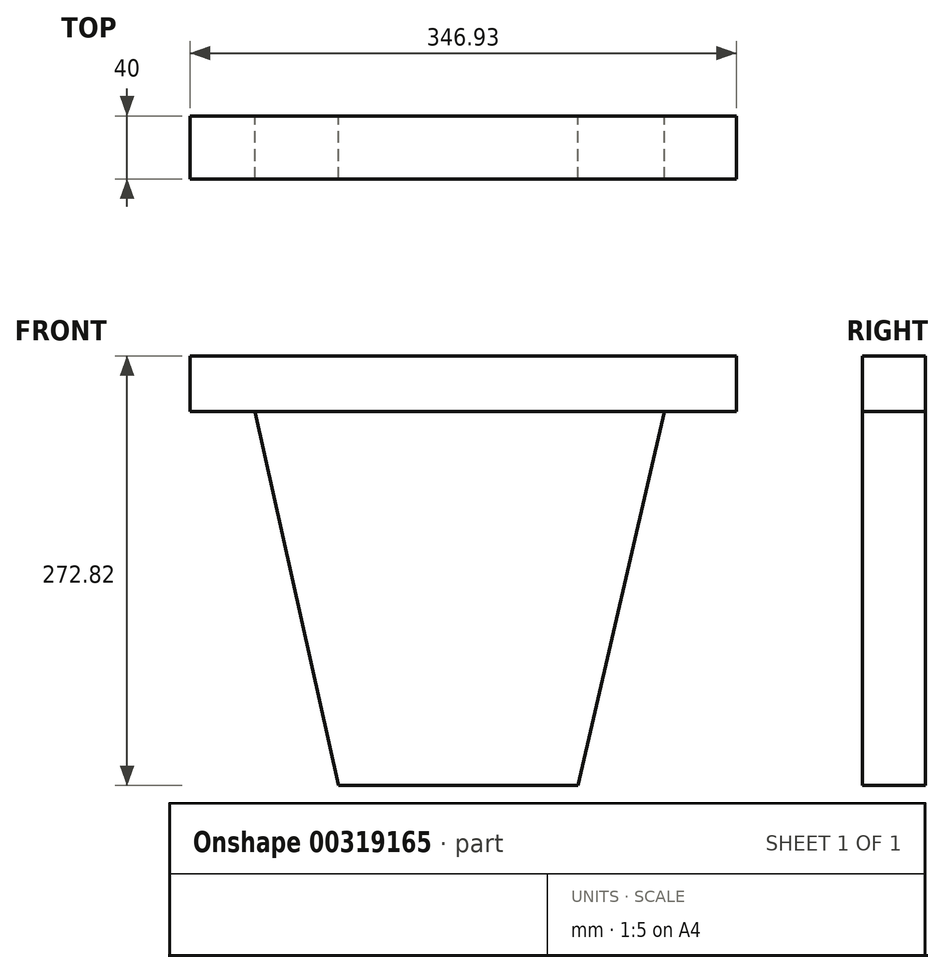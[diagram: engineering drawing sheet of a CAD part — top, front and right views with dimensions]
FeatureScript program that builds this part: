
annotation { "Feature Type Name" : "Feature", "Feature Type Description" : "" }
export const myFeature = defineFeature(function(context is Context, id is Id, definition is map)
    precondition{}
    {
        {
            var Q0;
            Q0=qCreatedBy(makeId("Front.planeOp"),FACE);
            var sketch = newSketch(context, id + "F0", { "sketchPlane" : qUnion([Q0])});
            skLineSegment(sketch, "E0", {"start": v(0, 0) * mm, "end": v(0, 0) * mm});
            skLineSegment(sketch, "E1", {"start": v(76.12, -76.13) * mm, "end": v(-75.82, -76.13) * mm});
            skLineSegment(sketch, "E2", {"start": v(-128.8, 161) * mm, "end": v(-75.82, -76.13) * mm});
            skLineSegment(sketch, "E3", {"start": v(76.12, -76.13) * mm, "end": v(131.21, 161.54) * mm});
            skLineSegment(sketch, "E4", {"start": v(131.21, 161.54) * mm, "end": v(-128.8, 161) * mm});
            skLineSegment(sketch, "E5.bottom", {"start": v(176.77, 161.54) * mm, "end": v(-170.16, 161.54) * mm});
            skLineSegment(sketch, "E5.top", {"start": v(176.77, 196.69) * mm, "end": v(-170.16, 196.69) * mm});
            skLineSegment(sketch, "E5.left", {"start": v(176.77, 161.54) * mm, "end": v(176.77, 196.69) * mm});
            skLineSegment(sketch, "E5.right", {"start": v(-170.16, 161.54) * mm, "end": v(-170.16, 196.69) * mm});
            skLineSegment(sketch, "E6.bottom", {"start": v(-170.16, 196.69) * mm, "end": v(-170.16, 196.69) * mm});
            skLineSegment(sketch, "E6.top", {"start": v(-170.16, 161.54) * mm, "end": v(-170.16, 161.54) * mm});
            skLineSegment(sketch, "E6.left", {"start": v(-170.16, 196.69) * mm, "end": v(-170.16, 161.54) * mm});
            skLineSegment(sketch, "E6.right", {"start": v(-170.16, 196.69) * mm, "end": v(-170.16, 161.54) * mm});
            skSolve(sketch);
        }
        {
            var Q0;
            Q0=makeQuery(id+"F0.imprint","IMPRINT",FACE,{"disambiguationData":[TD([[makeQuery(id+"F0.imprint","IMPRINT",EDGE,{"derivedFrom":sQuery(id+"F0.wireOp",EDGE,"E5.top")}),1.0]])]});
            var sketch = newSketch(context, id + "F1", { "sketchPlane" : qUnion([Q0])});
            skLineSegment(sketch, "E7", {"start": v(0, 322.2) * mm, "end": v(-165.7, 189.35) * mm});
            skLineSegment(sketch, "E8", {"start": v(-165.7, 189.35) * mm, "end": v(0, 322.2) * mm});
            skLineSegment(sketch, "E9", {"start": v(0, 322.2) * mm, "end": v(184.62, 190.7) * mm});
            skLineSegment(sketch, "E10", {"start": v(184.62, 190.7) * mm, "end": v(184.62, 190.7) * mm});
            skPoint(sketch, "E11", {"position": v(92.31, 256.44) * mm});
            skPoint(sketch, "E12", {"position": v(104.66, 247.65) * mm});
            skPoint(sketch, "E13", {"position": v(-25.1, 334.05) * mm});
            skPoint(sketch, "E14", {"position": v(-31.78, 296.72) * mm});
            skSolve(sketch);
        }
        {
            var Q0;
            {var subQ0=sQuery(id+"F1.wireOp",EDGE,"E9");var subQ1=sQuery(id+"F1.wireOp",EDGE,"E8");var subQ2=makeQuery(id+"F1.imprint","INTERSECT",VERTEX,{"derivedFrom":[subQ1,subQ0]});Q0=makeQuery(id+"F1.imprint","IMPRINT",FACE,{"disambiguationData":[TD([[makeQuery(id+"F1.imprint","IMPRINT",EDGE,{"disambiguationData":[TD([[subQ2,1.0]])],"derivedFrom":subQ1}),-1.0]])]});}
            var Q1;
            Q1=makeQuery(id+"F0.imprint","IMPRINT",FACE,{"disambiguationData":[TD([[makeQuery(id+"F0.imprint","IMPRINT",EDGE,{"derivedFrom":sQuery(id+"F0.wireOp",EDGE,"E5.top")}),1.0]])]});
            var Q2;
            Q2=makeQuery(id+"F0.imprint","IMPRINT",FACE,{"disambiguationData":[TD([[makeQuery(id+"F0.imprint","IMPRINT",EDGE,{"derivedFrom":sQuery(id+"F0.wireOp",EDGE,"E1")}),-1.0]])]});
            extrude(context, id + "F2", {"entities" : qUnion([Q0, Q1, Q2]), "endBound" : BoundingType.SYMMETRIC, "depth" : 40 * mm});
        }
    });
